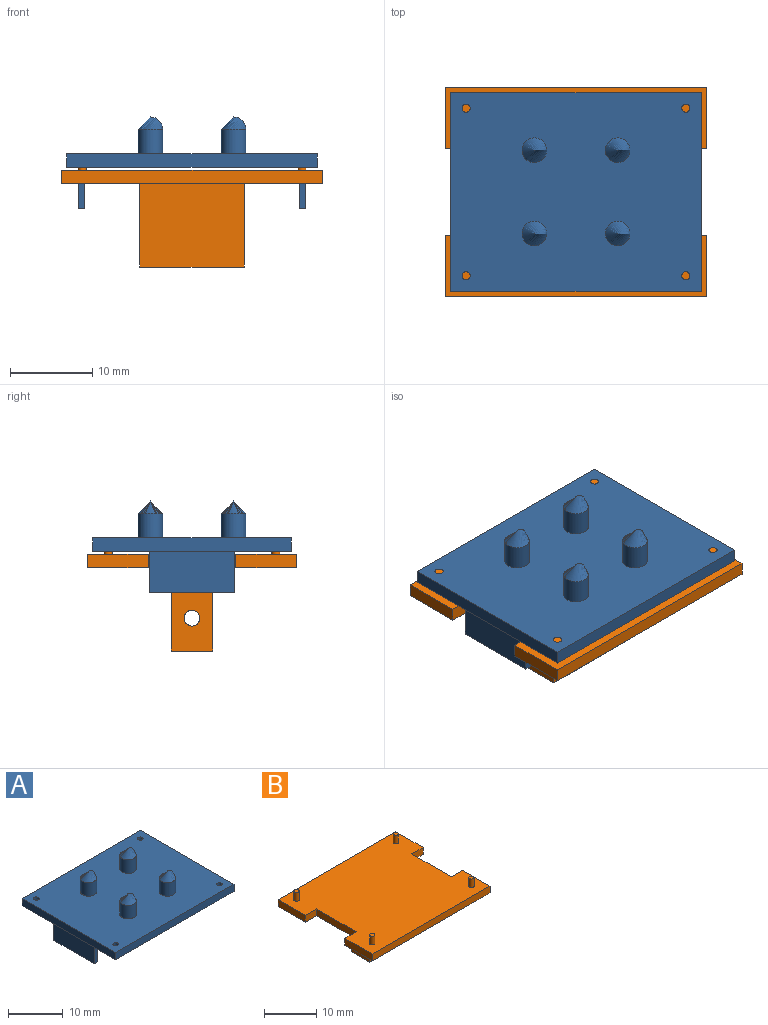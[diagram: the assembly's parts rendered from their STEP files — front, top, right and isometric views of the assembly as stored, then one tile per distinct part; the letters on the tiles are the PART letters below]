
ASSEMBLY  parts=2 mates=1
PART A: 32 faces, bbox 30.5x24.1x11.1 mm
  f0: plane 30.48x1.6mm, normal (0,1,0), area 48.8mm2, adj f1,f3,f4,f5
  f1: plane 24.13x1.6mm, normal (-1,0,0), area 38.6mm2, adj f0,f2,f4,f5
  f2: plane 30.48x1.6mm, normal (0,-1,0), area 48.8mm2, adj f1,f3,f4,f5
  f3: plane 24.13x1.6mm, normal (1,0,0), area 38.6mm2, adj f0,f2,f4,f5
  f4: plane 30.48x24.13mm, normal (0,0,1), area 704.1mm2, adj f0,f1,f2,f3,f6,f7,f8,f9
  f5: plane 30.48x24.13mm, normal (0,0,-1), area 715.7mm2, adj f0,f1,f2,f3,f6,f7,f8,f9
  f6: cylinder r=0.5mm len=1.6mm, axis (0,0,1), area 5mm2, adj f4,f5
  f7: cylinder r=0.5mm len=1.6mm, axis (0,0,1), area 5mm2, adj f4,f5
  f8: cylinder r=0.5mm len=1.6mm, axis (0,0,1), area 5mm2, adj f4,f5
  f9: cylinder r=0.5mm len=1.6mm, axis (0,0,1), area 5mm2, adj f4,f5
  f10: plane 5x0.8mm, normal (0,-1,0), area 4mm2, adj f5,f11,f13,f14
  f11: plane 10.43x5mm, normal (-1,0,0), area 52.1mm2, adj f5,f10,f12,f14
  f12: plane 5x0.8mm, normal (0,1,0), area 4mm2, adj f5,f11,f13,f14
  f13: plane 10.43x5mm, normal (1,0,0), area 52.1mm2, adj f5,f10,f12,f14
  f14: plane 10.43x0.8mm, normal (0,0,-1), area 8.3mm2, adj f10,f11,f12,f13
  f15: plane 5x0.8mm, normal (0,-1,0), area 4mm2, adj f5,f16,f18,f19
  f16: plane 10.43x5mm, normal (-1,0,0), area 52.1mm2, adj f5,f15,f17,f19
  f17: plane 5x0.8mm, normal (0,1,0), area 4mm2, adj f5,f16,f18,f19
  f18: plane 10.43x5mm, normal (1,0,0), area 52.1mm2, adj f5,f15,f17,f19
  f19: plane 10.43x0.8mm, normal (0,0,-1), area 8.3mm2, adj f15,f16,f17,f18
  f20: cylinder r=1.5mm len=3mm, axis (0,0,-1), area 28.3mm2, adj f4,f31
  f21: plane 0x0mm, normal (0,0,1), area 0mm2, adj f31
  f22: cylinder r=1.5mm len=3mm, axis (0,0,-1), area 28.3mm2, adj f4,f30
  f23: plane 0x0mm, normal (0,0,1), area 0mm2, adj f30
  f24: cylinder r=1.5mm len=3mm, axis (0,0,-1), area 28.3mm2, adj f4,f29
  f25: plane 0x0mm, normal (0,0,1), area 0mm2, adj f29
  f26: cylinder r=1.5mm len=3mm, axis (0,0,-1), area 28.3mm2, adj f4,f28
  f27: plane 0x0mm, normal (0,0,1), area 0mm2, adj f28
  f28: torus R=0mm, axis (0,0,1), area 14.1mm2, adj f26,f27
  f29: torus R=0mm, axis (0,0,1), area 14.1mm2, adj f24,f25
  f30: torus R=0mm, axis (0,0,1), area 14.1mm2, adj f22,f23
  f31: torus R=0mm, axis (0,0,1), area 14.1mm2, adj f20,f21
PART B: 28 faces, bbox 31.8x25.4x13.8 mm
  f0: plane 7.37x1.6mm, normal (-1,0,0), area 11.8mm2, adj f2,f3,f6,f26
  f1: plane 7.37x1.6mm, normal (1,0,0), area 11.8mm2, adj f2,f3,f6,f22
  f2: plane 31.75x25.4mm, normal (0,0,1), area 738.3mm2, adj f0,f1,f4,f5,f6,f7,f8,f10
  f3: plane 31.75x25.4mm, normal (0,0,-1), area 676.9mm2, adj f0,f1,f4,f5,f6,f7,f16,f17
  f4: plane 31.75x1.6mm, normal (0,1,0), area 50.8mm2, adj f2,f3,f5,f7
  f5: plane 7.37x1.6mm, normal (-1,0,0), area 11.8mm2, adj f2,f3,f4,f25
  f6: plane 31.75x1.6mm, normal (0,-1,0), area 50.8mm2, adj f0,f1,f2,f3
  f7: plane 7.37x1.6mm, normal (1,0,0), area 11.8mm2, adj f2,f3,f4,f23
  f8: cylinder r=0.5mm len=2mm, axis (0,0,-1), area 6.3mm2, adj f2,f9
  f9: plane 1x1mm, normal (0,0,1), area 0.8mm2, adj f8
  f10: cylinder r=0.5mm len=2mm, axis (0,0,-1), area 6.3mm2, adj f2,f11
  f11: plane 1x1mm, normal (0,0,1), area 0.8mm2, adj f10
  f12: cylinder r=0.5mm len=2mm, axis (0,0,-1), area 6.3mm2, adj f2,f13
  f13: plane 1x1mm, normal (0,0,1), area 0.8mm2, adj f12
  f14: cylinder r=0.5mm len=2mm, axis (0,0,-1), area 6.3mm2, adj f2,f15
  f15: plane 1x1mm, normal (0,0,1), area 0.8mm2, adj f14
  f16: plane 10.16x5.08mm, normal (1,0,0), area 48.7mm2, adj f3,f17,f19,f20,f21
  f17: plane 12.7x10.16mm, normal (0,-1,0), area 129mm2, adj f3,f16,f18,f20
  f18: plane 10.16x5.08mm, normal (-1,0,0), area 48.7mm2, adj f3,f17,f19,f20,f21
  f19: plane 12.7x10.16mm, normal (0,1,0), area 129mm2, adj f3,f16,f18,f20
  f20: plane 12.7x5.08mm, normal (0,0,-1), area 64.5mm2, adj f16,f17,f18,f19
  f21: cylinder r=0.96mm len=12.7mm, axis (-1,0,0), area 76.5mm2, adj f16,f18
  f22: plane 3.05x1.6mm, normal (0,1,0), area 4.9mm2, adj f1,f2,f3,f24
  f23: plane 3.05x1.6mm, normal (0,-1,0), area 4.9mm2, adj f2,f3,f7,f24
  f24: plane 10.67x1.6mm, normal (1,0,0), area 17.1mm2, adj f2,f3,f22,f23
  f25: plane 3.05x1.6mm, normal (0,-1,0), area 4.9mm2, adj f2,f3,f5,f27
  f26: plane 3.05x1.6mm, normal (0,1,0), area 4.9mm2, adj f0,f2,f3,f27
  f27: plane 10.67x1.6mm, normal (-1,0,0), area 17.1mm2, adj f2,f3,f25,f26
PLACE A t=(-1.23,-8.55,13.29)mm
PLACE B rot(axis=(1,0,0),0deg) t=(-1.23,-8.55,11.29)mm
MATE fastened B.f14 <-> A.f9  axis (0,0,1) through (12.15,1.65,14.89)mm
